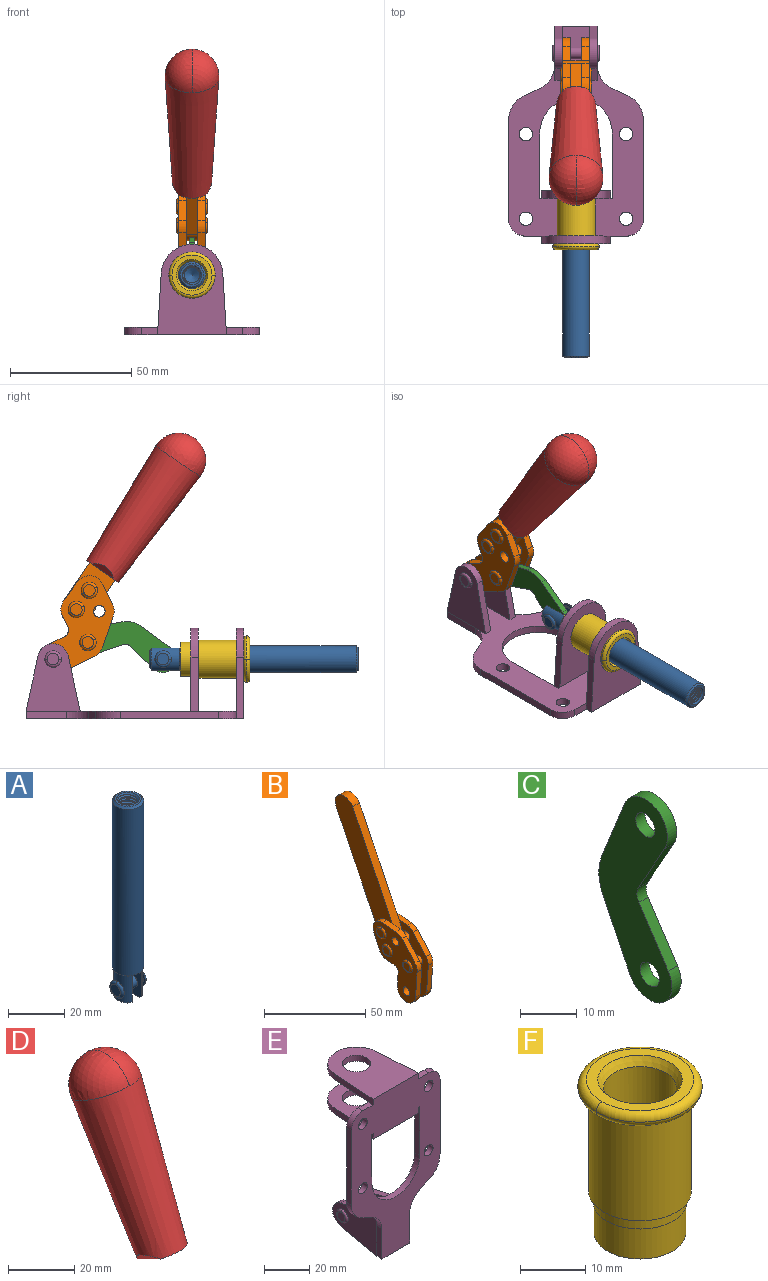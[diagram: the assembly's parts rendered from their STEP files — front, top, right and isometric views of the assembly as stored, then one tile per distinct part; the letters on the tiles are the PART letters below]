
ASSEMBLY  parts=6 mates=6
PART A: 48 faces, bbox 12.6x11.1x86.1 mm
  f0: torus R=2.41mm, axis (-1,0,0), area 15mm2, adj f30,f32,f34
  f1: torus R=2.41mm, axis (-1,0,0), area 15mm2, adj f29,f31,f33
  f2: cylinder r=5.54mm len=72.39mm, axis (0,0,1), area 2518.5mm2, adj f3,f4,f42,f43
  f3: cone r=5.54mm half-angle=45deg, axis (0,0,1), area 7.6mm2, adj f2,f5,f41
  f4: cone r=5.54mm half-angle=45deg, axis (0,0,-1), area 34.9mm2, adj f2,f39
  f5: cylinder r=5.08mm len=11.48mm, axis (0,0,1), area 108.3mm2, adj f3,f7,f8,f41
  f6: cylinder r=2.41mm len=4.83mm, axis (-1,0,0), area 71.2mm2, adj f40,f41
  f7: cylinder r=2.41mm len=4.83mm, axis (-1,0,0), area 7.6mm2, adj f5,f34
  f8: cone r=5.08mm half-angle=45deg, axis (0,0,1), area 10.6mm2, adj f5,f37,f41
  f9: cone r=3.98mm half-angle=45deg, axis (0,0,1), area 17.6mm2, adj f27,f39,f45,f46,f47
  f10: cylinder r=2.41mm len=4.83mm, axis (-1,0,0), area 7.6mm2, adj f33,f38
  f11: cylinder r=3.2mm len=6.4mm, axis (0,0,1), area 78.4mm2, adj f12,f28,f44,f45,f47
  f12: cylinder r=3.2mm len=6.4mm, axis (0,0,1), area 10.5mm2, adj f11,f13,f45,f47
  f13: cylinder r=3.2mm len=6.4mm, axis (0,0,1), area 10.5mm2, adj f12,f14,f45,f47
  f14: cylinder r=3.2mm len=6.4mm, axis (0,0,1), area 10.5mm2, adj f13,f15,f45,f47
  f15: cylinder r=3.2mm len=6.4mm, axis (0,0,1), area 10.5mm2, adj f14,f16,f45,f47
  f16: cylinder r=3.2mm len=6.4mm, axis (0,0,1), area 10.5mm2, adj f15,f17,f45,f47
  f17: cylinder r=3.2mm len=6.4mm, axis (0,0,1), area 10.5mm2, adj f16,f18,f45,f47
  f18: cylinder r=3.2mm len=6.4mm, axis (0,0,1), area 10.5mm2, adj f17,f19,f45,f47
  f19: cylinder r=3.2mm len=6.4mm, axis (0,0,1), area 10.5mm2, adj f18,f20,f45,f47
  f20: cylinder r=3.2mm len=6.4mm, axis (0,0,1), area 10.5mm2, adj f19,f21,f45,f47
  f21: cylinder r=3.2mm len=6.4mm, axis (0,0,1), area 10.5mm2, adj f20,f22,f45,f47
  f22: cylinder r=3.2mm len=6.4mm, axis (0,0,1), area 10.5mm2, adj f21,f23,f45,f47
  f23: cylinder r=3.2mm len=6.4mm, axis (0,0,1), area 10.5mm2, adj f22,f24,f45,f47
  f24: cylinder r=3.2mm len=6.4mm, axis (0,0,1), area 10.5mm2, adj f23,f25,f45,f47
  f25: cylinder r=3.2mm len=6.4mm, axis (0,0,1), area 10.5mm2, adj f24,f26,f45,f47
  f26: cylinder r=3.2mm len=6.4mm, axis (0,0,1), area 10.5mm2, adj f25,f27,f45,f47
  f27: cylinder r=3.2mm len=6.4mm, axis (0,0,1), area 7.4mm2, adj f9,f26,f45,f47
  f28: cone r=3.2mm half-angle=60deg, axis (0,0,1), area 37.2mm2, adj f11
  f29: plane 4.83x4.83mm, normal (-1,0,0), area 18.3mm2, adj f1,f31
  f30: plane 4.83x4.83mm, normal (1,0,0), area 18.3mm2, adj f0,f32
  f31: torus R=2.41mm, axis (-1,0,0), area 15mm2, adj f1,f29,f33
  f32: torus R=2.41mm, axis (-1,0,0), area 15mm2, adj f0,f30,f34
  f33: plane 6.83x6.83mm, normal (1,0,0), area 18.3mm2, adj f1,f10,f31
  f34: plane 6.83x6.83mm, normal (-1,0,0), area 18.3mm2, adj f0,f7,f32
  f35: cone r=5.08mm half-angle=45deg, axis (0,0,1), area 10.6mm2, adj f36,f38,f40
  f36: plane 7.25x1.97mm, normal (0,0,-1), area 10mm2, adj f35,f40
  f37: plane 7.25x1.97mm, normal (0,0,-1), area 10mm2, adj f8,f41
  f38: cylinder r=5.08mm len=11.48mm, axis (0,0,1), area 108.3mm2, adj f10,f35,f40,f42
  f39: plane 9.55x9.55mm, normal (0,0,1), area 22mm2, adj f4,f9
  f40: plane 12.76x10.09mm, normal (1,0,0), area 95.7mm2, adj f6,f35,f36,f38,f42,f43
  f41: plane 12.76x10.09mm, normal (-1,0,0), area 95.7mm2, adj f3,f5,f6,f8,f37,f43
  f42: cone r=5.54mm half-angle=45deg, axis (0,0,1), area 7.6mm2, adj f2,f38,f40
  f43: plane 11.07x4.7mm, normal (0,0,-1), area 50.4mm2, adj f2,f40,f41
  f44: plane 0.89x0.62mm, normal (-1,0,0), area 0.3mm2, adj f11,f45,f46,f47
  f45: bspline ~24.8x7.63mm, area 266.6mm2, adj f9,f11,f12,f13,f14,f15,f16,f17
  f46: bspline ~24.87x7.63mm, area 73.6mm2, adj f9,f44,f45,f47
  f47: bspline ~24.98x7.63mm, area 272.5mm2, adj f9,f11,f12,f13,f14,f15,f16,f17
PART B: 59 faces, bbox 12.9x60.2x99.6 mm
  f0: torus R=2.39mm, axis (-1,0,0), area 14.9mm2, adj f20,f43,f51
  f1: torus R=2.39mm, axis (-1,0,0), area 14.9mm2, adj f19,f42,f51
  f2: torus R=2.39mm, axis (-1,0,0), area 14.9mm2, adj f18,f35,f51
  f3: torus R=2.39mm, axis (-1,0,0), area 14.9mm2, adj f14,f17,f23
  f4: torus R=2.39mm, axis (-1,0,0), area 14.9mm2, adj f13,f16,f23
  f5: torus R=2.39mm, axis (-1,0,0), area 14.9mm2, adj f12,f15,f23
  f6: cylinder r=2.39mm len=4.78mm, axis (1,0,0), area 46.5mm2, adj f48,f50,f51
  f7: cylinder r=2.39mm len=4.78mm, axis (1,0,0), area 46.5mm2, adj f50,f51
  f8: cylinder r=6.35mm len=12.68mm, axis (1,0,0), area 61.8mm2, adj f38,f39,f50,f51
  f9: cylinder r=2.39mm len=4.78mm, axis (-1,0,0), area 70.5mm2, adj f46,f50
  f10: cylinder r=2.39mm len=4.78mm, axis (-1,0,0), area 46.5mm2, adj f23,f45,f46
  f11: cylinder r=2.39mm len=4.78mm, axis (-1,0,0), area 46.5mm2, adj f23,f46
  f12: plane 4.78x4.78mm, normal (1,0,0), area 17.9mm2, adj f5,f15
  f13: plane 4.78x4.78mm, normal (1,0,0), area 17.9mm2, adj f4,f16
  f14: plane 4.78x4.78mm, normal (1,0,0), area 17.9mm2, adj f3,f17
  f15: torus R=2.39mm, axis (-1,0,0), area 14.9mm2, adj f5,f12,f23
  f16: torus R=2.39mm, axis (-1,0,0), area 14.9mm2, adj f4,f13,f23
  f17: torus R=2.39mm, axis (-1,0,0), area 14.9mm2, adj f3,f14,f23
  f18: plane 4.78x4.78mm, normal (-1,0,0), area 17.9mm2, adj f2,f35
  f19: plane 4.78x4.78mm, normal (-1,0,0), area 17.9mm2, adj f1,f42
  f20: plane 4.78x4.78mm, normal (-1,0,0), area 17.9mm2, adj f0,f43
  f21: plane 2.26x0.2mm, normal (1,0,0), area 0.2mm2, adj f31,f44
  f22: plane 2.26x0.2mm, normal (-1,0,0), area 0.2mm2, adj f41,f44
  f23: plane 39.37x30.77mm, normal (1,0,0), area 565.5mm2, adj f3,f4,f5,f10,f11,f15,f16,f17
  f24: cylinder r=6.1mm len=4.15mm, axis (-1,0,0), area 14.7mm2, adj f23,f25,f32,f46
  f25: plane 10.25x9.01mm, normal (0,-0.75,0.66), area 42.3mm2, adj f23,f24,f26,f46
  f26: cylinder r=6.35mm len=4.64mm, axis (-1,0,0), area 15.6mm2, adj f23,f25,f27,f46
  f27: plane 15.84x3.1mm, normal (0,-1,-0.07), area 49.2mm2, adj f23,f26,f28,f46
  f28: cylinder r=6.35mm len=12.68mm, axis (-1,0,0), area 61.8mm2, adj f23,f27,f29,f46
  f29: plane 8.11x3.1mm, normal (0,1,0.07), area 25.2mm2, adj f23,f28,f30,f46
  f30: cylinder r=3.05mm len=3.25mm, axis (-1,0,0), area 14.8mm2, adj f23,f29,f31,f46
  f31: plane 5.99x3.1mm, normal (0,0.07,-1), area 18.6mm2, adj f21,f23,f30,f44,f46
  f32: plane 9.5x3.1mm, normal (0,-0.07,1), area 29.5mm2, adj f23,f24,f33,f46,f47
  f33: cylinder r=6.1mm len=8.63mm, axis (-1,0,0), area 39.1mm2, adj f23,f32,f34,f47
  f34: plane 8.65x3.96mm, normal (0,0.91,-0.42), area 29.5mm2, adj f23,f33,f44,f47
  f35: torus R=2.39mm, axis (-1,0,0), area 14.9mm2, adj f2,f18,f51
  f36: plane 10.25x9.01mm, normal (0,-0.75,0.66), area 42.3mm2, adj f37,f49,f50,f51
  f37: cylinder r=6.35mm len=4.64mm, axis (1,0,0), area 15.6mm2, adj f36,f38,f50,f51
  f38: plane 15.84x3.1mm, normal (0,-1,-0.07), area 49.2mm2, adj f8,f37,f50,f51
  f39: plane 8.11x3.1mm, normal (0,1,0.07), area 25.2mm2, adj f8,f40,f50,f51
  f40: cylinder r=3.05mm len=3.25mm, axis (1,0,0), area 14.8mm2, adj f39,f41,f50,f51
  f41: plane 5.99x3.1mm, normal (0,0.07,-1), area 18.6mm2, adj f22,f40,f44,f50,f51
  f42: torus R=2.39mm, axis (-1,0,0), area 14.9mm2, adj f1,f19,f51
  f43: torus R=2.39mm, axis (-1,0,0), area 14.9mm2, adj f0,f20,f51
  f44: cylinder r=6.35mm len=12.12mm, axis (-1,0,0), area 128.9mm2, adj f21,f22,f23,f31,f34,f41,f46,f47
  f45: plane 2.65x1.35mm, normal (1,0,0), area 1mm2, adj f10,f55
  f46: plane 39.08x20.42mm, normal (-1,0,0), area 412.5mm2, adj f9,f10,f11,f24,f25,f26,f27,f28
  f47: plane 77.62x39.82mm, normal (1,0,0), area 850mm2, adj f32,f33,f34,f44,f53,f54,f55
  f48: plane 2.65x1.35mm, normal (-1,0,0), area 1mm2, adj f6,f55
  f49: cylinder r=6.1mm len=4.15mm, axis (1,0,0), area 14.7mm2, adj f36,f50,f51,f56
  f50: plane 39.08x20.42mm, normal (1,0,0), area 412.5mm2, adj f6,f7,f8,f9,f36,f37,f38,f39
  f51: plane 39.37x30.77mm, normal (-1,0,0), area 565.5mm2, adj f0,f1,f2,f6,f7,f8,f35,f36
  f52: plane 8.65x3.96mm, normal (0,0.91,-0.42), area 29.5mm2, adj f44,f51,f57,f58
  f53: plane 68.49x33.4mm, normal (0,0.9,-0.44), area 358.1mm2, adj f44,f47,f54,f58
  f54: cylinder r=6.35mm len=12.06mm, axis (1,0,0), area 93.7mm2, adj f47,f53,f55,f58
  f55: plane 68.49x33.4mm, normal (0,-0.9,0.44), area 358.1mm2, adj f44,f45,f46,f47,f48,f50,f54,f58
  f56: plane 9.5x3.1mm, normal (0,-0.07,1), area 29.5mm2, adj f49,f50,f51,f57,f58
  f57: cylinder r=6.1mm len=8.63mm, axis (1,0,0), area 39.1mm2, adj f51,f52,f56,f58
  f58: plane 77.62x39.82mm, normal (-1,0,0), area 850mm2, adj f44,f52,f53,f54,f55,f56,f57
PART C: 12 faces, bbox 2.3x18.2x42.8 mm
  f0: cylinder r=2.4mm len=4.8mm, axis (1,0,0), area 34.9mm2, adj f4,f11
  f1: cylinder r=10.41mm len=8.47mm, axis (1,0,0), area 20.2mm2, adj f4,f9,f10,f11
  f2: cylinder r=3.05mm len=3.16mm, axis (1,0,0), area 7.7mm2, adj f4,f6,f7,f11
  f3: cylinder r=2.4mm len=4.8mm, axis (1,0,0), area 34.9mm2, adj f4,f11
  f4: plane 42.81x18.23mm, normal (-1,0,0), area 414.1mm2, adj f0,f1,f2,f3,f5,f6,f7,f8
  f5: cylinder r=5.54mm len=10.67mm, axis (1,0,0), area 41.8mm2, adj f4,f6,f10,f11
  f6: plane 11.66x6.53mm, normal (0,-0.87,-0.49), area 30.9mm2, adj f2,f4,f5,f11
  f7: plane 11.17x7.33mm, normal (0,-0.84,0.55), area 30.9mm2, adj f2,f4,f8,f11
  f8: cylinder r=5.54mm len=10.51mm, axis (1,0,0), area 41.8mm2, adj f4,f7,f9,f11
  f9: plane 13.67x6.67mm, normal (0,0.9,-0.44), area 35.1mm2, adj f1,f4,f8,f11
  f10: plane 14.1x5.7mm, normal (0,0.93,0.37), area 35.1mm2, adj f1,f4,f5,f11
  f11: plane 42.81x18.23mm, normal (1,0,0), area 414.1mm2, adj f0,f1,f2,f3,f5,f6,f7,f8
PART D: 11 faces, bbox 22.3x42.6x64.5 mm
  f0: sphere r=11.13mm, area 411.4mm2, adj f1,f8
  f1: cone r=11.11mm half-angle=3.3deg, axis (0,0.44,0.9), area 3251.8mm2, adj f0,f7,f8,f9,f10
  f2: cylinder r=6.16mm len=11.7mm, axis (1,0,0), area 89.5mm2, adj f3,f4,f5,f6
  f3: plane 60.23x36.75mm, normal (-1,0,0), area 763.6mm2, adj f2,f4,f6,f10
  f4: plane 51.37x25.05mm, normal (0,0.9,-0.44), area 264.2mm2, adj f2,f3,f5,f10
  f5: plane 60.23x36.75mm, normal (1,0,0), area 763.6mm2, adj f2,f4,f6,f10
  f6: plane 51.37x25.05mm, normal (0,-0.9,0.44), area 264.2mm2, adj f2,f3,f5,f10
  f7: plane 9.95x5.95mm, normal (0.71,-0.31,-0.64), area 25.8mm2, adj f1,f10
  f8: sphere r=11.13mm, area 411.4mm2, adj f0,f1
  f9: plane 9.95x5.95mm, normal (-0.71,-0.31,-0.64), area 25.8mm2, adj f1,f10
  f10: plane 14.27x11.38mm, normal (0,-0.44,-0.9), area 106.7mm2, adj f1,f3,f4,f5,f6,f7,f9
PART E: 55 faces, bbox 55.7x37.4x89.8 mm
  f0: torus R=2.41mm, axis (-1,0,0), area 15mm2, adj f11,f15,f25
  f1: torus R=2.41mm, axis (-1,0,0), area 15mm2, adj f10,f12,f22
  f2: cylinder r=2.78mm len=5.56mm, axis (0,-1,0), area 54.2mm2, adj f30,f54
  f3: cylinder r=14.99mm len=29.97mm, axis (0,-1,0), area 145.9mm2, adj f30,f49,f53,f54
  f4: cylinder r=2.78mm len=5.56mm, axis (0,-1,0), area 54.2mm2, adj f30,f54
  f5: cylinder r=2.78mm len=5.56mm, axis (0,-1,0), area 54.2mm2, adj f30,f54
  f6: cylinder r=2.78mm len=5.56mm, axis (0,-1,0), area 54.2mm2, adj f30,f54
  f7: cylinder r=6.35mm len=12.7mm, axis (0,0,1), area 123.6mm2, adj f27,f51
  f8: cylinder r=6.35mm len=12.7mm, axis (0,0,-1), area 124.7mm2, adj f21,f35
  f9: cylinder r=2.41mm len=11.18mm, axis (-1,0,0), area 169.4mm2, adj f16,f19
  f10: plane 4.83x4.83mm, normal (1,0,0), area 18.3mm2, adj f1,f12
  f11: plane 4.83x4.83mm, normal (-1,0,0), area 18.3mm2, adj f0,f15
  f12: torus R=2.41mm, axis (-1,0,0), area 15mm2, adj f1,f10,f22
  f13: cylinder r=6.35mm len=12.41mm, axis (1,0,0), area 53.4mm2, adj f18,f19,f22,f23
  f14: cylinder r=6.35mm len=12.41mm, axis (-1,0,0), area 53.4mm2, adj f16,f17,f24,f25
  f15: torus R=2.41mm, axis (-1,0,0), area 15mm2, adj f0,f11,f25
  f16: plane 27.86x22.35mm, normal (1,0,0), area 425.4mm2, adj f9,f14,f17,f24,f30
  f17: plane 22.86x4.97mm, normal (0,0.21,0.98), area 72.5mm2, adj f14,f16,f25,f30
  f18: plane 22.86x4.97mm, normal (0,0.21,0.98), area 72.5mm2, adj f13,f19,f22,f30
  f19: plane 27.86x22.35mm, normal (-1,0,0), area 425.4mm2, adj f9,f13,f18,f23,f30
  f20: cylinder r=12.7mm len=25.35mm, axis (0,0,-1), area 119.8mm2, adj f21,f34,f35,f36
  f21: plane 34.21x28.07mm, normal (0,0,-1), area 702.4mm2, adj f8,f20,f30,f34,f36
  f22: plane 27.96x22.45mm, normal (1,0,0), area 407.2mm2, adj f1,f12,f13,f18,f23,f30,f42,f43
  f23: plane 22.86x4.97mm, normal (0,0.21,-0.98), area 72.5mm2, adj f13,f19,f22,f44
  f24: plane 22.86x4.97mm, normal (0,0.21,-0.98), area 72.5mm2, adj f14,f16,f25,f44
  f25: plane 27.86x22.35mm, normal (-1,0,0), area 407.1mm2, adj f0,f14,f15,f17,f24,f30,f45,f46
  f26: plane 3.1x0.95mm, normal (0,0,-1), area 2.7mm2, adj f30,f49,f50,f54
  f27: plane 34.21x28.07mm, normal (0,0,1), area 702.4mm2, adj f7,f28,f30,f50,f52
  f28: cylinder r=12.7mm len=25.35mm, axis (0,0,1), area 118.8mm2, adj f27,f50,f51,f52
  f29: plane 3.1x0.95mm, normal (0,0,-1), area 2.7mm2, adj f30,f52,f53,f54
  f30: plane 86.54x55.63mm, normal (0,1,0), area 2362.9mm2, adj f2,f3,f4,f5,f6,f16,f17,f18
  f31: plane 40.56x3.1mm, normal (-1,0,0), area 125.7mm2, adj f30,f32,f48,f54
  f32: cylinder r=7.11mm len=7.11mm, axis (0,-1,0), area 34.6mm2, adj f30,f31,f33,f54
  f33: plane 6.67x3.1mm, normal (0,0,1), area 20.4mm2, adj f30,f32,f34,f54
  f34: plane 25.39x3.13mm, normal (-1,0.06,0), area 79.5mm2, adj f20,f21,f33,f35,f54
  f35: plane 37.31x28.45mm, normal (0,0,1), area 789.9mm2, adj f8,f20,f34,f36,f54
  f36: plane 25.39x3.13mm, normal (1,0.06,0), area 79.5mm2, adj f20,f21,f35,f37,f54
  f37: plane 6.67x3.1mm, normal (0,0,1), area 20.4mm2, adj f30,f36,f38,f54
  f38: cylinder r=7.11mm len=7.11mm, axis (0,-1,0), area 34.6mm2, adj f30,f37,f39,f54
  f39: plane 40.56x3.1mm, normal (1,0,0), area 125.7mm2, adj f30,f38,f40,f54
  f40: cylinder r=11.18mm len=10.16mm, axis (0,-1,0), area 39.5mm2, adj f30,f39,f41,f54
  f41: plane 6.09x3.1mm, normal (0.42,0,-0.91), area 20.8mm2, adj f30,f40,f42,f54
  f42: cylinder r=11.18mm len=9.41mm, axis (0,-1,0), area 37.2mm2, adj f22,f30,f41,f43,f54
  f43: plane 16.5x3.1mm, normal (1,0,0), area 51.1mm2, adj f22,f42,f44,f54
  f44: plane 17.37x3.1mm, normal (0,0,-1), area 53.8mm2, adj f23,f24,f30,f43,f45,f54
  f45: plane 16.5x3.1mm, normal (-1,0,0), area 51.1mm2, adj f25,f44,f46,f54
  f46: cylinder r=11.18mm len=9.41mm, axis (0,-1,0), area 37.2mm2, adj f25,f30,f45,f47,f54
  f47: plane 6.09x3.1mm, normal (-0.42,0,-0.91), area 20.8mm2, adj f30,f46,f48,f54
  f48: cylinder r=11.18mm len=10.16mm, axis (0,-1,0), area 39.5mm2, adj f30,f31,f47,f54
  f49: plane 26.54x3.1mm, normal (-1,0,0), area 82.3mm2, adj f3,f26,f30,f54
  f50: plane 25.39x3.1mm, normal (1,0.06,0), area 78.8mm2, adj f26,f27,f28,f51,f54
  f51: plane 37.31x28.45mm, normal (0,0,-1), area 789.9mm2, adj f7,f28,f50,f52,f54
  f52: plane 25.39x3.1mm, normal (-1,0.06,0), area 78.8mm2, adj f27,f28,f29,f51,f54
  f53: plane 26.54x3.1mm, normal (1,0,0), area 82.3mm2, adj f3,f29,f30,f54
  f54: plane 89.66x55.63mm, normal (0,-1,0), area 2678.5mm2, adj f2,f3,f4,f5,f6,f26,f29,f31
PART F: 15 faces, bbox 20.6x20.6x28.7 mm
  f0: torus R=8.26mm, axis (0,0,1), area 56.8mm2, adj f1,f10,f12
  f1: torus R=8.26mm, axis (0,0,1), area 56.8mm2, adj f0,f6,f13
  f2: cylinder r=5.59mm len=25.91mm, axis (0,0,1), area 909.6mm2, adj f3,f4
  f3: cone r=6.86mm half-angle=45deg, axis (0,0,-1), area 70.2mm2, adj f2,f14
  f4: cone r=6.47mm half-angle=30deg, axis (0,0,1), area 66.7mm2, adj f2,f13
  f5: cylinder r=7.04mm len=14.07mm, axis (0,0,1), area 252.6mm2, adj f11,f14
  f6: torus R=8.26mm, axis (0,0,1), area 56.8mm2, adj f1,f12,f13
  f7: cylinder r=7.16mm len=14.33mm, axis (0,0,1), area 91.5mm2, adj f9,f11
  f8: cylinder r=7.86mm len=18.42mm, axis (0,0,1), area 909.6mm2, adj f9,f10
  f9: plane 15.72x15.72mm, normal (0,0,-1), area 33mm2, adj f7,f8
  f10: plane 16.51x16.51mm, normal (0,0,-1), area 19.9mm2, adj f0,f8,f12
  f11: plane 14.33x14.33mm, normal (0,0,-1), area 5.7mm2, adj f5,f7
  f12: torus R=8.26mm, axis (0,0,1), area 56.8mm2, adj f0,f6,f10
  f13: plane 16.51x16.51mm, normal (0,0,1), area 82.7mm2, adj f1,f4,f6
  f14: plane 14.07x14.07mm, normal (0,0,-1), area 7.8mm2, adj f3,f5
PLACE A rot(axis=(1,0,0),90deg) t=(-15.2,13.27,-2.99)mm
PLACE B rot(axis=(1,0,0),60.4deg) t=(-15.2,3.05,16.06)mm
PLACE C rot(axis=(1,0,0),104.5deg) t=(-15.2,18.93,1.66)mm
PLACE D rot(axis=(1,0,0),60.4deg) t=(-15.2,3.05,16.06)mm
PLACE E rot(axis=(1,0,0),90deg) t=(-15.2,11.02,-2.99)mm fixed
PLACE F rot(axis=(1,0,0),90deg) t=(-15.2,11.02,-2.99)mm
MATE revolute C.f3 <-> B.f4  axis (1,0,0) through (-15.2,28.79,28.48)mm
MATE revolute E.f0 <-> B.f7  axis (-1,0,0) through (-15.2,43.11,21.62)mm
MATE fastened E.f7 <-> F.f0  axis (0,-1,0) through (-15.2,-35.37,21.62)mm
MATE fastened B.f54 <-> D.f2  axis (1,0,0) through (-15.2,-9.51,104.88)mm
MATE slider A.f2 <-> E.f7  axis (0,-1,0) through (-15.2,-45.51,21.62)mm
MATE revolute A.f6 <-> C.f5  axis (-1,0,0) through (-15.2,-2.21,21.62)mm
